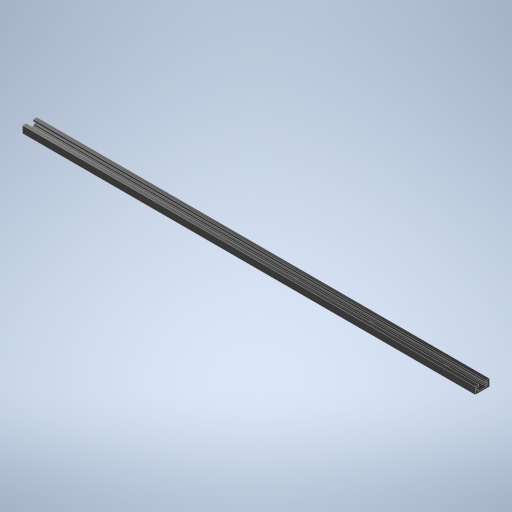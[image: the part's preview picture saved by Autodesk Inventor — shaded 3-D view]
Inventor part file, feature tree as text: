
AUTODESK INVENTOR PART (.ipt)
format: ipt  version: 2024 (Build 280153000, 153)  size: 293,888 bytes
history: native  units: in
note: dims shown in document units (in); Inventor stores cm internally (conversion verified against a paired STEP export)
features: extrude x2, sketch x2, projected_geometry x1
ambient origin geometry x8: Origin, YZ Plane, XZ Plane, XY Plane, X Axis, Y Axis, Z Axis, Center Point
bodies: Solid1 (feature_tree)
feature tree (5):
  extrude  "Extrusion1"  Depth=0.375in
  extrude  "Extrusion2"  Depth=0.2812in
  sketch  "Sketch1"  dims[d3=24.0in d4=0.0in d20=0.375in]
  sketch  "Sketch2"  dims[d21=0.75in d22=0.2812in d23=0.1562in d24=0.2812in d25=0.1875in d26=0.2188in d27=2.0in d28=4.0in d29=4.0in d30=8.0in d31=0.3125in d32=0.3125in d33=0.3125in d34=0.0in d35=0.0in d36=0.5in d37=0.0344in d38=0.5in d39=0.0344in]
  projected_geometry  "Projected Loop1"
